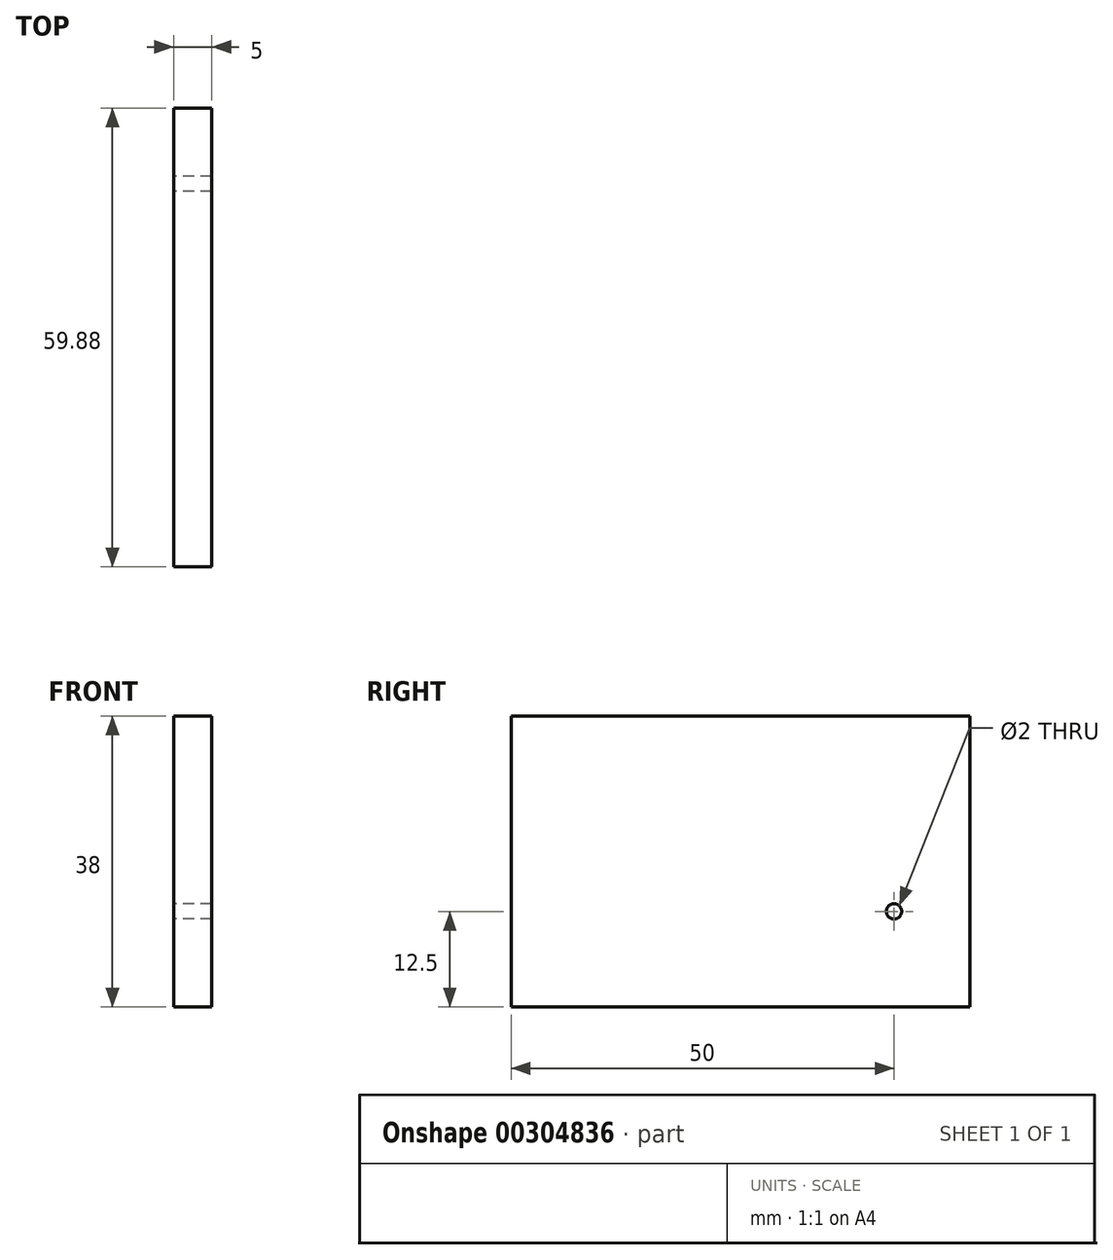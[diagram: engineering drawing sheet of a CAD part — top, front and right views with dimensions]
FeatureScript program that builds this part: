
annotation { "Feature Type Name" : "Feature", "Feature Type Description" : "" }
export const myFeature = defineFeature(function(context is Context, id is Id, definition is map)
    precondition{}
    {
        {
            var Q0;
            Q0=qCreatedBy(makeId("Right.planeOp"),FACE);
            var sketch = newSketch(context, id + "F0", { "sketchPlane" : qUnion([Q0])});
            skLineSegment(sketch, "E0.bottom", {"start": v(25, -19) * mm, "end": v(-25, -19) * mm});
            skLineSegment(sketch, "E0.top", {"start": v(25, 19) * mm, "end": v(-25, 19) * mm});
            skLineSegment(sketch, "E0.left", {"start": v(25, -19) * mm, "end": v(25, 19) * mm});
            skLineSegment(sketch, "E0.right", {"start": v(-25, -19) * mm, "end": v(-25, 19) * mm});
            skPoint(sketch, "E0.middle", {"position": v(0, 0) * mm});
            skLineSegment(sketch, "E1.bottom", {"start": v(34.88, -19) * mm, "end": v(15.12, -19) * mm});
            skLineSegment(sketch, "E1.top", {"start": v(34.88, 19) * mm, "end": v(15.12, 19) * mm});
            skLineSegment(sketch, "E1.left", {"start": v(34.88, -19) * mm, "end": v(34.88, 19) * mm});
            skLineSegment(sketch, "E1.right", {"start": v(15.12, -19) * mm, "end": v(15.12, 19) * mm});
            skPoint(sketch, "E1.middle", {"position": v(25, 0) * mm});
            skLineSegment(sketch, "E2", {"start": v(25, 0) * mm, "end": v(25, -6.5) * mm});
            skCircle(sketch, "E3", {"center": v(25, -6.5) * mm, "radius": 1 * mm});
            skSolve(sketch);
        }
        {
            var Q0;
            {var subQ0=sQuery(id+"F0.wireOp",EDGE,"E1.right");Q0=makeQuery(id+"F0.imprint","IMPRINT",FACE,{"disambiguationData":[TD([[makeQuery(id+"F0.imprint","IMPRINT",EDGE,{"derivedFrom":subQ0}),-1.0]])]});}
            var Q1;
            {var subQ3=sQuery(id+"F0.wireOp",EDGE,"E1.left");Q1=makeQuery(id+"F0.imprint","IMPRINT",FACE,{"disambiguationData":[TD([[makeQuery(id+"F0.imprint","IMPRINT",EDGE,{"derivedFrom":subQ3}),1.0]])]});}
            var Q2;
            Q2=makeQuery(id+"F0.imprint","IMPRINT",FACE,{"disambiguationData":[TD([[makeQuery(id+"F0.imprint","IMPRINT",EDGE,{"derivedFrom":sQuery(id+"F0.wireOp",EDGE,"E0.bottom")}),-1.0]])]});
            extrude(context, id + "F1", {"entities" : qUnion([Q0, Q1, Q2]), "depth" : 5 * mm});
        }
    });
